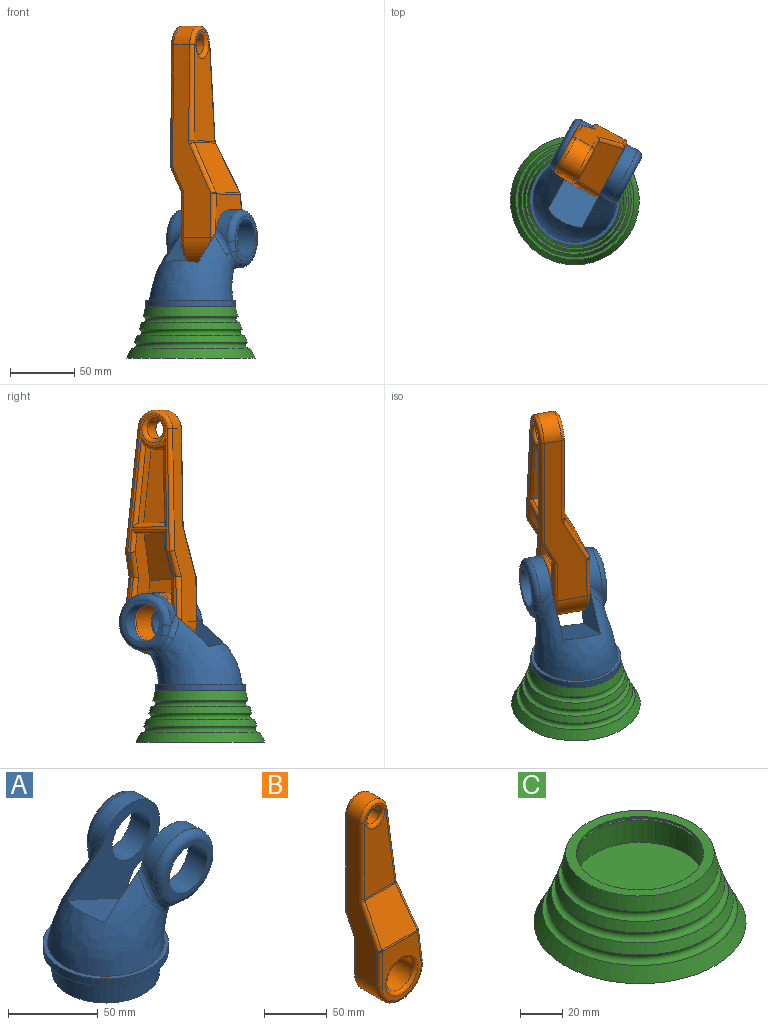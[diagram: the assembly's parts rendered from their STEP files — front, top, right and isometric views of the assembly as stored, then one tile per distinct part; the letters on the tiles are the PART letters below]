
ASSEMBLY  parts=3 mates=2
PART A: 29 faces, bbox 95.6x71.2x93.5 mm
  f0: bspline ~81.29x65mm, area 5808.1mm2, adj f2,f3,f5,f11,f12,f13,f14,f24
  f1: cylinder r=22.5mm len=45mm, axis (0,1,0), area 1015.6mm2, adj f2,f3,f15,f24
  f2: bspline ~21.91x19.31mm, area 111.9mm2, adj f0,f1,f14,f17,f24
  f3: bspline ~24.51x21.07mm, area 112.3mm2, adj f0,f1,f14,f16,f24
  f4: cylinder r=15mm len=30mm, axis (0,-1,0), area 1413.7mm2, adj f10,f24
  f5: plane 70x70mm, normal (0,0,1), area 530.2mm2, adj f0,f6
  f6: cylinder r=35mm len=70mm, axis (0,0,-1), area 1099.6mm2, adj f5,f7
  f7: plane 70x70mm, normal (0,0,-1), area 1021mm2, adj f6,f28
  f8: cylinder r=22.5mm len=45mm, axis (0,1,0), area 1015.6mm2, adj f11,f13,f21,f25
  f9: plane 35x35mm, normal (0,-1,0), area 286.2mm2, adj f19,f20,f21,f22,f23
  f10: plane 35x35mm, normal (0,1,0), area 286.2mm2, adj f4,f15,f16,f17,f18
  f11: bspline ~24.51x21.07mm, area 112.3mm2, adj f0,f8,f12,f19,f25
  f12: bspline ~17.12x16.29mm, area 73.1mm2, adj f0,f11,f13,f20
  f13: bspline ~21.91x19.31mm, area 111.9mm2, adj f0,f8,f12,f22,f25
  f14: bspline ~17.68x16.44mm, area 73.1mm2, adj f0,f2,f3,f18
  f15: torus R=17.5mm, axis (0,-1,0), area 797.9mm2, adj f1,f10,f16,f17
  f16: bspline ~13.16x7.21mm, area 53.8mm2, adj f3,f10,f15,f18
  f17: bspline ~13.9x7.88mm, area 51.4mm2, adj f2,f10,f15,f18
  f18: bspline ~11.88x11.8mm, area 57mm2, adj f10,f14,f16,f17
  f19: bspline ~14.1x7.65mm, area 53.8mm2, adj f9,f11,f20,f21
  f20: bspline ~12.15x12.07mm, area 57mm2, adj f9,f12,f19,f22
  f21: torus R=17.5mm, axis (0,-1,0), area 797.9mm2, adj f8,f9,f19,f22
  f22: bspline ~12.67x6.97mm, area 51.4mm2, adj f9,f13,f20,f21
  f23: cylinder r=15mm len=30mm, axis (0,-1,0), area 1413.7mm2, adj f9,f25
  f24: plane 73.4x62.85mm, normal (0,-1,0), area 1806.7mm2, adj f0,f1,f2,f3,f4,f26
  f25: plane 73.4x62.85mm, normal (0,1,0), area 1806.7mm2, adj f0,f8,f11,f13,f23,f26
  f26: plane 54.18x31.24mm, normal (0.42,0,0.91), area 1671.4mm2, adj f0,f24,f25
  f27: plane 60x60mm, normal (0,0,-1), area 2827.4mm2, adj f28
  f28: cylinder r=30mm len=60mm, axis (0,0,1), area 2827.4mm2, adj f7,f27
PART B: 62 faces, bbox 54.1x40x193.3 mm
  f0: plane 59.06x9mm, normal (1,0,0), area 531.5mm2, adj f19,f20,f22,f34
  f1: plane 60.11x9mm, normal (-0.99,0,-0.13), area 545.8mm2, adj f19,f20,f22,f33
  f2: plane 36x29.72mm, normal (0,0.89,-0.45), area 1099.1mm2, adj f16,f17,f18,f23
  f3: plane 107.01x36.83mm, normal (0,1,0), area 546mm2, adj f5,f6,f27,f29,f31,f32,f33,f34
  f4: plane 57.02x44.01mm, normal (0,1,0), area 511.3mm2, adj f5,f6,f24,f26,f28,f37,f58,f59
  f5: plane 20.02x10.01mm, normal (0,0.89,-0.45), area 45.1mm2, adj f3,f4,f24,f25,f27,f59
  f6: plane 20x10mm, normal (0,0.89,-0.45), area 44.7mm2, adj f3,f4,f30,f56
  f7: plane 150x34mm, normal (-1,0,0), area 2728.9mm2, adj f10,f11,f40,f45,f47,f50,f54,f56
  f8: plane 56.29x44mm, normal (0,-1,0), area 1179mm2, adj f36,f40,f41,f43,f44
  f9: plane 148.67x34mm, normal (0.99,0,0.13), area 2705.1mm2, adj f10,f11,f43,f48,f51,f53,f57,f59
  f10: cylinder r=15mm len=29.87mm, axis (0,1,0), area 631.8mm2, adj f7,f9,f52,f55
  f11: cylinder r=25mm len=50mm, axis (0,1,0), area 1964.8mm2, adj f7,f9,f41,f60
  f12: plane 86.29x34.06mm, normal (0,-1,0), area 2040.4mm2, adj f38,f49,f50,f52,f53
  f13: plane 39.6x38.73mm, normal (0,-0.89,0.45), area 1602.7mm2, adj f44,f45,f48,f49
  f14: cylinder r=7.5mm len=15mm, axis (0,1,0), area 659.7mm2, adj f38,f39
  f15: cylinder r=15mm len=30mm, axis (0,1,0), area 2261.9mm2, adj f36,f37
  f16: plane 53.62x29mm, normal (1,0,0), area 928.8mm2, adj f2,f17,f21,f23,f28,f30,f31
  f17: plane 31.79x17.62mm, normal (0,1,0), area 369.9mm2, adj f2,f16,f18,f21
  f18: plane 51.5x29mm, normal (-0.99,0,-0.13), area 900.5mm2, adj f2,f17,f21,f23,f24,f25,f27
  f19: plane 60.11x23.82mm, normal (0,1,0), area 1158.7mm2, adj f0,f1,f20,f22
  f20: cylinder r=15.5mm len=15.77mm, axis (0,1,0), area 149.3mm2, adj f0,f1,f19,f32
  f21: cylinder r=23mm len=31.79mm, axis (0,1,0), area 668.8mm2, adj f16,f17,f18,f26
  f22: plane 23.82x9mm, normal (0,0,1), area 214.4mm2, adj f0,f1,f19,f35
  f23: plane 24.9x11mm, normal (0,0,-1), area 273.9mm2, adj f2,f16,f18,f29
  f24: cylinder r=3mm len=33.45mm, axis (0.13,0,-0.99), area 99.4mm2, adj f4,f5,f18,f25,f26
  f25: cylinder r=3mm len=21.6mm, axis (0.12,-0.44,-0.89), area 102.1mm2, adj f5,f18,f24,f27
  f26: torus R=20mm, axis (0,-1,0), area 191.3mm2, adj f4,f21,f24,f28
  f27: cylinder r=3mm len=17.51mm, axis (0.13,0,-0.99), area 72.2mm2, adj f3,f5,f18,f25,f29
  f28: cylinder r=3mm len=35.71mm, axis (0,0,-1), area 110.5mm2, adj f4,f16,f26,f30
  f29: cylinder r=3mm len=30.52mm, axis (1,0,0), area 127mm2, adj f3,f23,f27,f31
  f30: cylinder r=3mm len=21.98mm, axis (0,-0.45,-0.89), area 105.4mm2, adj f6,f16,f28,f31
  f31: cylinder r=3mm len=17.11mm, axis (0,0,1), area 70.4mm2, adj f3,f16,f29,f30
  f32: torus R=12.5mm, axis (0,-1,0), area 90.8mm2, adj f3,f20,f33,f34
  f33: cylinder r=3mm len=70.18mm, axis (0.13,0,-0.99), area 301.3mm2, adj f1,f3,f32,f35
  f34: cylinder r=3mm len=68.39mm, axis (0,0,1), area 293.1mm2, adj f0,f3,f32,f35
  f35: cylinder r=3mm len=30.25mm, axis (-1,0,0), area 123.3mm2, adj f3,f22,f33,f34
  f36: torus R=18mm, axis (0,-1,0), area 476.4mm2, adj f8,f15
  f37: torus R=18mm, axis (0,-1,0), area 476.4mm2, adj f4,f15
  f38: torus R=10.5mm, axis (0,1,0), area 254.3mm2, adj f12,f14
  f39: torus R=10.5mm, axis (0,-1,0), area 254.3mm2, adj f3,f14
  f40: cylinder r=3mm len=34.29mm, axis (0,0,1), area 161.6mm2, adj f7,f8,f41,f42
  f41: torus R=22mm, axis (0,-1,0), area 369mm2, adj f8,f11,f40,f43
  f42: sphere r=3mm, area 4.2mm2, adj f40,f44,f45
  f43: cylinder r=3mm len=31.77mm, axis (0.13,0,-0.99), area 149.2mm2, adj f8,f9,f41,f46
  f44: cylinder r=3mm len=39.6mm, axis (1,0,0), area 55.1mm2, adj f8,f13,f42,f46
  f45: cylinder r=3mm len=40.07mm, axis (0,-0.45,-0.89), area 204.1mm2, adj f7,f13,f42,f47
  f46: sphere r=3mm, area 4mm2, adj f43,f44,f48
  f47: torus R=6mm, axis (1,0,0), area 8.9mm2, adj f7,f45,f49,f50
  f48: cylinder r=3mm len=39.71mm, axis (0.12,-0.44,-0.89), area 197.8mm2, adj f9,f13,f46,f51
  f49: cylinder r=3mm len=34.42mm, axis (1,0,0), area 47.6mm2, adj f12,f13,f47,f51
  f50: cylinder r=3mm len=74.29mm, axis (0,0,-1), area 350.1mm2, adj f7,f12,f47,f52
  f51: bspline ~4.27x3.55mm, area 8.9mm2, adj f9,f48,f49,f53
  f52: torus R=12mm, axis (0,1,0), area 197.2mm2, adj f10,f12,f50,f53
  f53: cylinder r=3mm len=76.28mm, axis (0.13,0,-0.99), area 360.8mm2, adj f9,f12,f51,f52
  f54: cylinder r=3mm len=95mm, axis (0,0,-1), area 446.5mm2, adj f3,f7,f55,f56
  f55: torus R=12mm, axis (0,-1,0), area 197.2mm2, adj f3,f10,f54,f57
  f56: cylinder r=3mm len=21.98mm, axis (0,0.45,0.89), area 105.4mm2, adj f6,f7,f54,f58
  f57: cylinder r=3mm len=96.98mm, axis (-0.13,0,0.99), area 458mm2, adj f3,f9,f55,f59
  f58: cylinder r=3mm len=35.71mm, axis (0,0,1), area 166.1mm2, adj f4,f7,f56,f60
  f59: cylinder r=3mm len=22.37mm, axis (-0.12,0.44,0.89), area 110.1mm2, adj f3,f4,f5,f9,f57,f61
  f60: torus R=22mm, axis (0,-1,0), area 369mm2, adj f4,f11,f58,f61
  f61: cylinder r=3mm len=33.19mm, axis (-0.13,0,0.99), area 153.8mm2, adj f4,f9,f59,f60
PART C: 15 faces, bbox 162.4x162.4x106.5 mm
  f0: torus R=37.56mm, axis (0,0,-1), area 1787.8mm2, adj f1,f14
  f1: torus R=181.52mm, axis (0,0,-1), area 1765mm2, adj f0,f2
  f2: plane 70x70mm, normal (0,0,1), area 1021mm2, adj f1,f3
  f3: cylinder r=30mm len=60mm, axis (0,0,-1), area 188.5mm2, adj f2,f4
  f4: plane 62x62mm, normal (0,0,-1), area 191.6mm2, adj f3,f5
  f5: cylinder r=31mm len=62mm, axis (0,0,-1), area 194.8mm2, adj f4,f6
  f6: plane 62x62mm, normal (0,0,1), area 191.6mm2, adj f5,f7
  f7: cylinder r=30mm len=60mm, axis (0,0,-1), area 2450.4mm2, adj f6,f8
  f8: plane 60x60mm, normal (0,0,1), area 2827.4mm2, adj f7
  f9: plane 100x100mm, normal (0,0,-1), area 7854mm2, adj f10
  f10: torus R=181.52mm, axis (0,0,-1), area 2619.1mm2, adj f9,f11
  f11: torus R=44.99mm, axis (0,0,-1), area 2160.5mm2, adj f10,f12
  f12: torus R=181.52mm, axis (0,0,-1), area 1566.5mm2, adj f11,f13
  f13: torus R=40.87mm, axis (0,0,-1), area 1953.8mm2, adj f12,f14
  f14: torus R=181.52mm, axis (0,0,-1), area 1361.3mm2, adj f0,f13
PLACE A rot(axis=(0,0,1),61.8deg) t=(1.9,-5.86,25.82)mm
PLACE B rot(axis=(-0.01,0.02,1),61.8deg) t=(-3.58,36.8,78.71)mm
PLACE C t=(1.9,-5.86,-14.18)mm fixed
MATE revolute C.f0 <-> A.f6  axis (0,0,1) through (1.9,-5.86,25.82)mm
MATE revolute A.f1 <-> B.f11  axis (0.88,-0.47,0) through (18.45,24.98,78.71)mm
